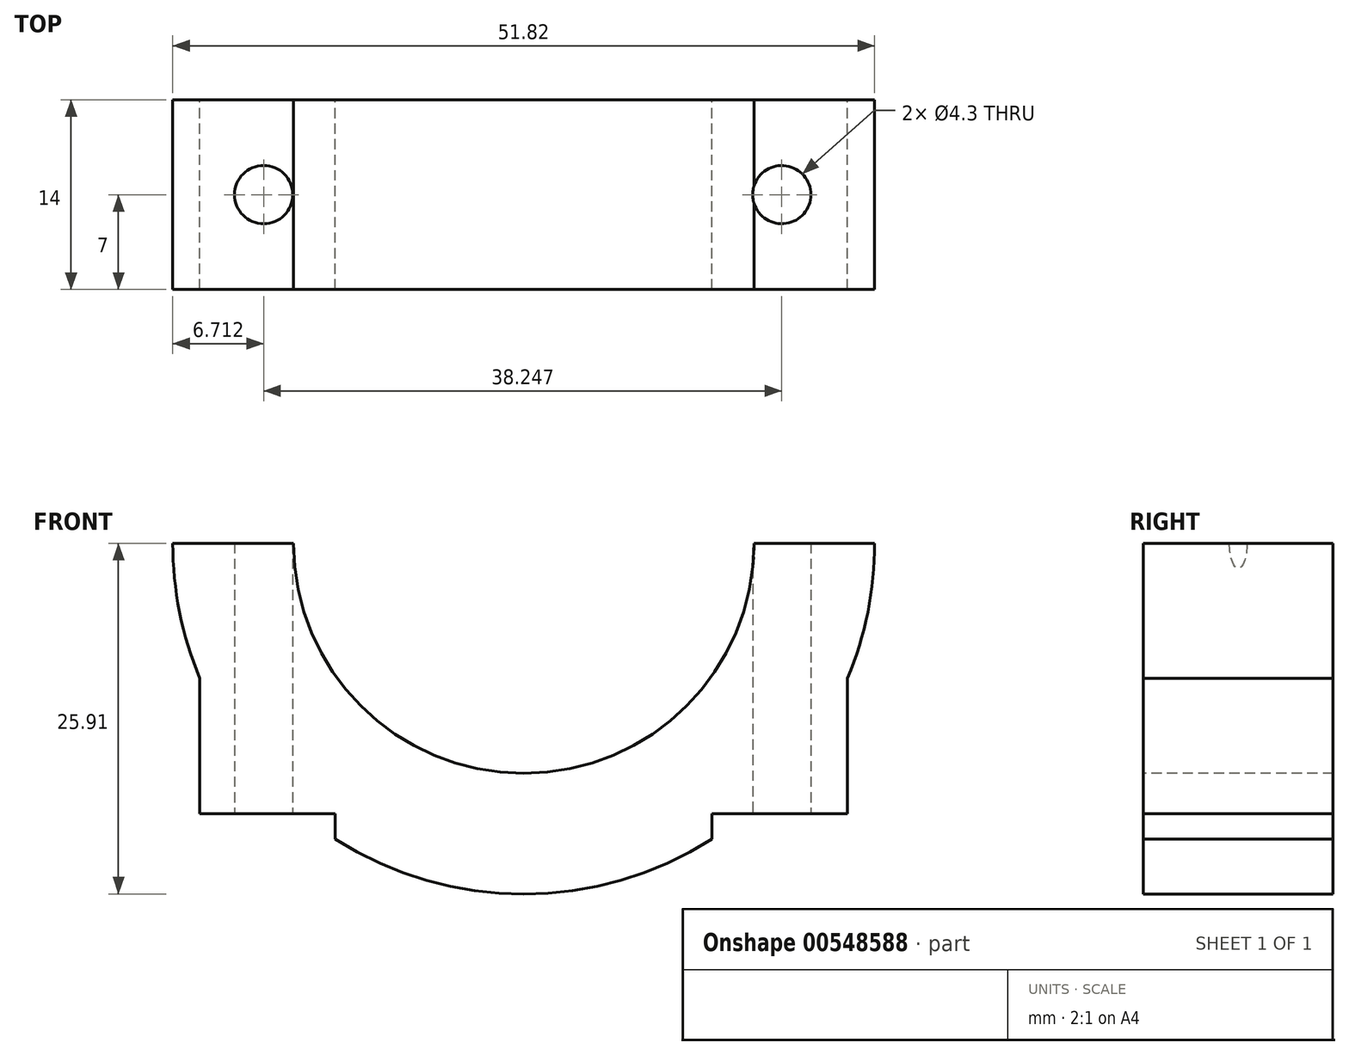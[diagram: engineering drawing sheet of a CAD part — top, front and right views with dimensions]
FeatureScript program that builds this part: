
annotation { "Feature Type Name" : "Feature", "Feature Type Description" : "" }
export const myFeature = defineFeature(function(context is Context, id is Id, definition is map)
    precondition{}
    {
        {
            var Q0;
            Q0=qCreatedBy(makeId("Front.planeOp"),FACE);
            var sketch = newSketch(context, id + "F0", { "sketchPlane" : qUnion([Q0])});
            skCircle(sketch, "E0", {"center": v(0, 0) * mm, "radius": 25.9 * mm});
            skSolve(sketch);
        }
        {
            var Q0;
            Q0=qSketchRegion(id+"F0",true);
            extrude(context, id + "F1", {"entities" : qUnion([Q0]), "depth" : 7 * mm, "offsetDistance" : 25 * mm, "hasSecondDirection" : true, "secondDirectionOppositeDirection" : true, "secondDirectionDepth" : 7 * mm});
        }
        {
            var Q0;
            Q0=qCreatedBy(makeId("Front.planeOp"),FACE);
            var sketch = newSketch(context, id + "F2", { "sketchPlane" : qUnion([Q0])});
            skCircle(sketch, "E1", {"center": v(0, 0) * mm, "radius": 17 * mm});
            skSolve(sketch);
        }
        {
            var Q0;
            Q0=qSketchRegion(id+"F2",true);
            extrude(context, id + "F3", {"entities" : qUnion([Q0]), "operationType" : NewBodyOperationType.REMOVE, "oppositeDirection" : true, "depth" : 7 * mm, "offsetDistance" : 25 * mm, "hasSecondDirection" : true, "secondDirectionOppositeDirection" : false, "secondDirectionDepth" : 7 * mm});
        }
        {
            var Q0;
            Q0=qCreatedBy(makeId("Top.planeOp"),FACE);
            var sketch = newSketch(context, id + "F4", { "sketchPlane" : qUnion([Q0])});
            skLineSegment(sketch, "E2.bottom", {"start": v(-62.72, 7) * mm, "end": v(62.72, 7) * mm});
            skLineSegment(sketch, "E2.top", {"start": v(-62.72, -7) * mm, "end": v(62.72, -7) * mm});
            skLineSegment(sketch, "E2.left", {"start": v(-62.72, 7) * mm, "end": v(-62.72, -7) * mm});
            skLineSegment(sketch, "E2.right", {"start": v(62.72, 7) * mm, "end": v(62.72, -7) * mm});
            skPoint(sketch, "E2.middle", {"position": v(0, 0) * mm});
            skSolve(sketch);
        }
        {
            var Q0;
            Q0=makeQuery(id+"F4.imprint","IMPRINT",FACE,{"disambiguationData":[TD([[makeQuery(id+"F4.imprint","IMPRINT",EDGE,{"derivedFrom":sQuery(id+"F4.wireOp",EDGE,"E2.bottom")}),-1.0]])]});
            var sketch = newSketch(context, id + "F5", { "sketchPlane" : qUnion([Q0])});
            skLineSegment(sketch, "E3.bottom", {"start": v(-15.9, 7) * mm, "end": v(-23.91, 7) * mm});
            skLineSegment(sketch, "E3.top", {"start": v(-15.9, -7) * mm, "end": v(-23.9, -7) * mm});
            skLineSegment(sketch, "E3.left", {"start": v(-15.9, 7) * mm, "end": v(-15.9, -7) * mm});
            skLineSegment(sketch, "E3.right", {"start": v(-23.91, 7) * mm, "end": v(-23.9, -7) * mm});
            skLineSegment(sketch, "E4.bottom", {"start": v(15.9, 7) * mm, "end": v(23.91, 7) * mm});
            skLineSegment(sketch, "E4.top", {"start": v(15.9, -7) * mm, "end": v(23.91, -7) * mm});
            skLineSegment(sketch, "E4.left", {"start": v(15.9, 7) * mm, "end": v(15.9, -7) * mm});
            skLineSegment(sketch, "E4.right", {"start": v(23.91, 7) * mm, "end": v(23.91, -7) * mm});
            skSolve(sketch);
        }
        {
            var Q0;
            Q0=qSketchRegion(id+"F5",true);
            extrude(context, id + "F6", {"entities" : qUnion([Q0]), "operationType" : NewBodyOperationType.ADD, "oppositeDirection" : true, "depth" : 20 * mm, "offsetDistance" : 25 * mm, "hasSecondDirection" : true, "secondDirectionOppositeDirection" : true, "secondDirectionDepth" : 6 * mm});
        }
        {
            var Q0;
            Q0=makeQuery(id+"F4.imprint","IMPRINT",FACE,{"disambiguationData":[TD([[makeQuery(id+"F4.imprint","IMPRINT",EDGE,{"derivedFrom":sQuery(id+"F4.wireOp",EDGE,"E2.bottom")}),-1.0]])]});
            var sketch = newSketch(context, id + "F7", { "sketchPlane" : qUnion([Q0])});
            skCircle(sketch, "E5", {"center": v(-19.2, 0) * mm, "radius": 2.15 * mm});
            skCircle(sketch, "E6", {"center": v(19.05, 0) * mm, "radius": 2.15 * mm});
            skSolve(sketch);
        }
        {
            var Q0;
            Q0=qSketchRegion(id+"F7",true);
            extrude(context, id + "F8", {"entities" : qUnion([Q0]), "operationType" : NewBodyOperationType.REMOVE, "depth" : 30 * mm, "offsetDistance" : 25 * mm, "hasSecondDirection" : true, "secondDirectionOppositeDirection" : true, "secondDirectionDepth" : 30 * mm});
        }
        {
            var Q0;
            Q0=makeQuery(id+"F6.opExtrude","CAP_FACE",FACE,{"disambiguationData":[OSD([sQuery(id+"F5.wireOp",EDGE,"E3.bottom"),sQuery(id+"F5.wireOp",EDGE,"E3.top"),sQuery(id+"F5.wireOp",EDGE,"E3.left"),sQuery(id+"F5.wireOp",EDGE,"E3.right")])],"isStart":false});
            var sketch = newSketch(context, id + "F9", { "sketchPlane" : qUnion([Q0])});
            skLineSegment(sketch, "E7.bottom", {"start": v(-23.91, -7) * mm, "end": v(-13.9, -7) * mm});
            skLineSegment(sketch, "E7.top", {"start": v(-23.91, 7) * mm, "end": v(-13.91, 7) * mm});
            skLineSegment(sketch, "E7.left", {"start": v(-23.91, -7) * mm, "end": v(-23.91, 7) * mm});
            skLineSegment(sketch, "E7.right", {"start": v(-13.9, -7) * mm, "end": v(-13.91, 7) * mm});
            skLineSegment(sketch, "E8.bottom", {"start": v(23.91, -7) * mm, "end": v(13.91, -7) * mm});
            skLineSegment(sketch, "E8.top", {"start": v(23.91, 7) * mm, "end": v(13.9, 7) * mm});
            skLineSegment(sketch, "E8.left", {"start": v(23.91, -7) * mm, "end": v(23.91, 7) * mm});
            skLineSegment(sketch, "E8.right", {"start": v(13.91, -7) * mm, "end": v(13.9, 7) * mm});
            skSolve(sketch);
        }
        {
            var Q0;
            Q0=qSketchRegion(id+"F9",true);
            extrude(context, id + "F10", {"entities" : qUnion([Q0]), "operationType" : NewBodyOperationType.REMOVE, "depth" : 10 * mm, "offsetDistance" : 25 * mm});
        }
        {
            var Q0;
            Q0=makeQuery(id+"F4.imprint","IMPRINT",FACE,{"disambiguationData":[TD([[makeQuery(id+"F4.imprint","IMPRINT",EDGE,{"derivedFrom":sQuery(id+"F4.wireOp",EDGE,"E2.bottom")}),-1.0]])]});
            var sketch = newSketch(context, id + "F11", { "sketchPlane" : qUnion([Q0])});
            skLineSegment(sketch, "E9.bottom", {"start": v(-37.76, 23.11) * mm, "end": v(37.76, 23.11) * mm});
            skLineSegment(sketch, "E9.top", {"start": v(-37.76, -23.11) * mm, "end": v(37.76, -23.11) * mm});
            skLineSegment(sketch, "E9.left", {"start": v(-37.76, 23.11) * mm, "end": v(-37.76, -23.11) * mm});
            skLineSegment(sketch, "E9.right", {"start": v(37.76, 23.11) * mm, "end": v(37.76, -23.11) * mm});
            skPoint(sketch, "E9.middle", {"position": v(0, 0) * mm});
            skSolve(sketch);
        }
        {
            var Q0;
            Q0 = qSketchRegion(id + "F11", true);
            extrude(context, id + "F12", {"entities" : qUnion([Q0]), "operationType" : NewBodyOperationType.REMOVE, "depth" : 30 * mm, "offsetDistance" : 25 * mm});
        }
    });
